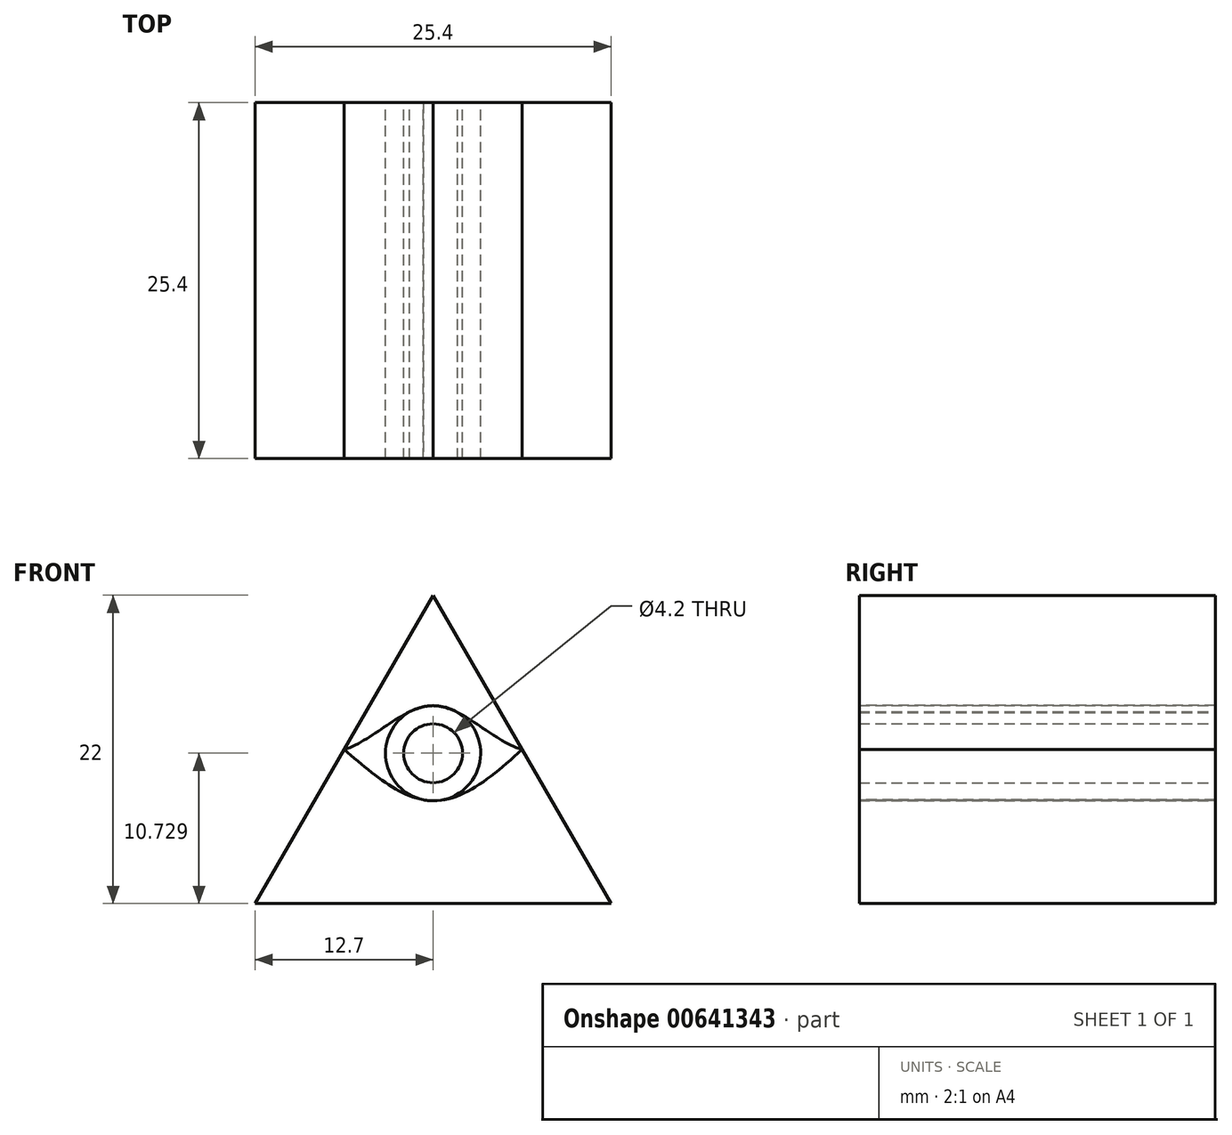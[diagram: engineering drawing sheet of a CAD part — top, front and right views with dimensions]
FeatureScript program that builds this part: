
annotation { "Feature Type Name" : "Feature", "Feature Type Description" : "" }
export const myFeature = defineFeature(function(context is Context, id is Id, definition is map)
    precondition{}
    {
        {
            var Q0;
            Q0=qCreatedBy(makeId("Front.planeOp"),FACE);
            var sketch = newSketch(context, id + "F0", { "sketchPlane" : qUnion([Q0])});
            skLineSegment(sketch, "E0.0", {"start": v(0, 0) * mm, "end": v(-25.4, 0) * mm});
            skLineSegment(sketch, "E0.1", {"start": v(-25.4, 0) * mm, "end": v(-12.7, 22) * mm});
            skLineSegment(sketch, "E0.2", {"start": v(-12.7, 22) * mm, "end": v(0, 0) * mm});
            skPoint(sketch, "E0.0.midPoint", {"position": v(-12.7, 0) * mm});
            skFitSpline(sketch, "E1", {"points": [v(-19.05, 11) * mm, v(-12.7, 14.13) * mm, v(-6.35, 11) * mm], "startDerivative": vector(12.48, 3.67) * mm, "endDerivative": vector(12.92, -3.64) * mm});
            skLineSegment(sketch, "E2", {"start": v(-12.7, 7.33) * mm, "end": v(-12.7, 14.13) * mm, "construction": true});
            skFitSpline(sketch, "E3", {"points": [v(-19.05, 11) * mm, v(-12.7, 7.33) * mm, v(-6.35, 11) * mm], "startDerivative": vector(12.7, -11) * mm, "endDerivative": vector(12.78, 11.79) * mm});
            skCircle(sketch, "E4", {"center": v(-12.7, 10.73) * mm, "radius": 3.4 * mm});
            skCircle(sketch, "E5", {"center": v(-12.7, 10.73) * mm, "radius": 2.1 * mm});
            skSolve(sketch);
        }
        {
            var Q0;
            {var subQ1=sQuery(id+"F0.wireOp",EDGE,"E1");var subQ3=sQuery(id+"F0.wireOp",EDGE,"E4");var subQ4=makeQuery(id+"F0.imprint","INTERSECT",VERTEX,{"disambiguationData":[OD(2.0)],"derivedFrom":[subQ1,subQ3]});Q0=makeQuery(id+"F0.imprint","IMPRINT",FACE,{"disambiguationData":[TD([[makeQuery(id+"F0.imprint","IMPRINT",EDGE,{"disambiguationData":[TD([[subQ4,1.0]])],"derivedFrom":subQ3}),-1.0]])]});}
            var Q1;
            {var subQ1=sQuery(id+"F0.wireOp",EDGE,"E1");var subQ3=sQuery(id+"F0.wireOp",EDGE,"E4");var subQ4=makeQuery(id+"F0.imprint","INTERSECT",VERTEX,{"disambiguationData":[OD(0.0)],"derivedFrom":[subQ1,subQ3]});Q1=makeQuery(id+"F0.imprint","IMPRINT",FACE,{"disambiguationData":[TD([[makeQuery(id+"F0.imprint","IMPRINT",EDGE,{"disambiguationData":[TD([[subQ4,-1.0]])],"derivedFrom":subQ3}),-1.0]])]});}
            extrude(context, id + "F1", {"entities" : qUnion([Q0, Q1]), "depth" : 25.4 * mm, "offsetDistance" : 25.4 * mm});
        }
        {
            var Q0;
            {var subQ7=sQuery(id+"F0.wireOp",EDGE,"E0.0");Q0=makeQuery(id+"F0.imprint","IMPRINT",FACE,{"disambiguationData":[TD([[makeQuery(id+"F0.imprint","IMPRINT",EDGE,{"derivedFrom":subQ7}),-1.0]])]});}
            var Q1;
            {var subQ1=sQuery(id+"F0.wireOp",EDGE,"E1");var subQ4=sQuery(id+"F0.wireOp",EDGE,"E4");var subQ10=makeQuery(id+"F0.imprint","INTERSECT",VERTEX,{"disambiguationData":[OD(1.0)],"derivedFrom":[subQ1,subQ4]});Q1=makeQuery(id+"F0.imprint","IMPRINT",FACE,{"disambiguationData":[TD([[makeQuery(id+"F0.imprint","IMPRINT",EDGE,{"disambiguationData":[TD([[subQ10,1.0]])],"derivedFrom":subQ4}),-1.0]])]});}
            extrude(context, id + "F2", {"entities" : qUnion([Q0, Q1]), "depth" : 25.4 * mm, "offsetDistance" : 25.4 * mm});
        }
        {
            var Q0;
            Q0=makeQuery(id+"F0.imprint","IMPRINT",FACE,{"disambiguationData":[TD([[makeQuery(id+"F0.imprint","IMPRINT",EDGE,{"derivedFrom":sQuery(id+"F0.wireOp",EDGE,"E5")}),-1.0]])]});
            extrude(context, id + "F3", {"entities" : qUnion([Q0]), "depth" : 25.4 * mm, "offsetDistance" : 25.4 * mm});
        }
        {
            var Q0;
            Q0=makeQuery(id+"F0.imprint","IMPRINT",FACE,{"disambiguationData":[TD([[makeQuery(id+"F0.imprint","IMPRINT",EDGE,{"derivedFrom":sQuery(id+"F0.wireOp",EDGE,"E5")}),1.0]])]});
            extrude(context, id + "F4", {"entities" : qUnion([Q0]), "depth" : 25.4 * mm, "offsetDistance" : 25.4 * mm});
        }
    });
